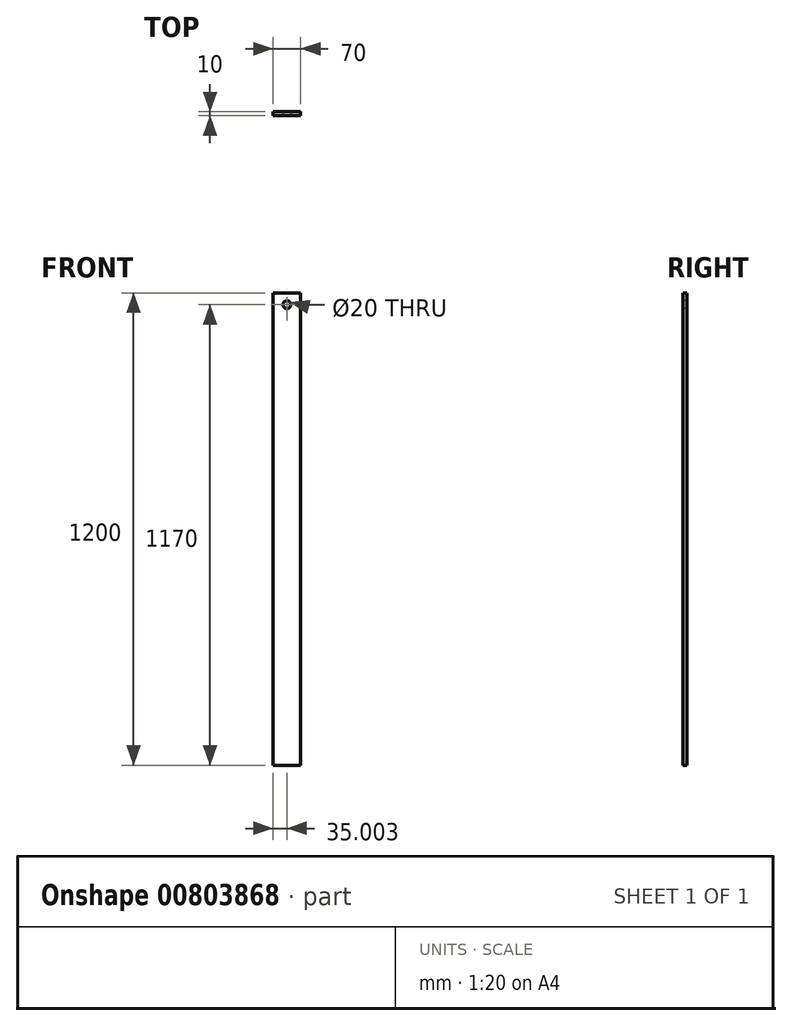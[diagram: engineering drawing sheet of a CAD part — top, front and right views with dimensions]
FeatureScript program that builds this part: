
annotation { "Feature Type Name" : "Feature", "Feature Type Description" : "" }
export const myFeature = defineFeature(function(context is Context, id is Id, definition is map)
    precondition{}
    {
        {
            var Q0;
            Q0=qCreatedBy(makeId("Top.planeOp"),FACE);
            var sketch = newSketch(context, id + "F0", { "sketchPlane" : qUnion([Q0])});
            skLineSegment(sketch, "E0.bottom", {"start": v(-11.05, 1.37) * mm, "end": v(58.95, 1.37) * mm});
            skLineSegment(sketch, "E0.top", {"start": v(-11.05, 11.37) * mm, "end": v(58.95, 11.37) * mm});
            skLineSegment(sketch, "E0.left", {"start": v(-11.05, 1.37) * mm, "end": v(-11.05, 11.37) * mm});
            skLineSegment(sketch, "E0.right", {"start": v(58.95, 1.37) * mm, "end": v(58.95, 11.37) * mm});
            skSolve(sketch);
        }
        {
            var Q0;
            Q0 = qSketchRegion(id + "F0", true);
            extrude(context, id + "F1", {"entities" : qUnion([Q0]), "depth" : 1200 * mm, "offsetDistance" : 25 * mm});
        }
        {
            var Q0;
            Q0=makeQuery(id+"F1.opExtrude","SWEPT_FACE",FACE,{"disambiguationData":[OSD([sQuery(id+"F0.wireOp",EDGE,"E0.bottom")])]});
            var sketch = newSketch(context, id + "F2", { "sketchPlane" : qUnion([Q0])});
            skCircle(sketch, "E1", {"center": v(23.95, 1170) * mm, "radius": 10 * mm});
            skPoint(sketch, "E1.centerSnap0", {"position": v(23.95, 1200) * mm});
            skSolve(sketch);
        }
        {
            var Q0;
            Q0=makeQuery(id+"F2.imprint","IMPRINT",FACE,{"disambiguationData":[TD([[makeQuery(id+"F2.imprint","IMPRINT",EDGE,{"derivedFrom":sQuery(id+"F2.wireOp",EDGE,"E1")}),1.0]])]});
            extrude(context, id + "F3", {"entities" : qUnion([Q0]), "operationType" : NewBodyOperationType.REMOVE, "oppositeDirection" : true, "depth" : 10 * mm, "offsetDistance" : 25 * mm});
        }
    });
